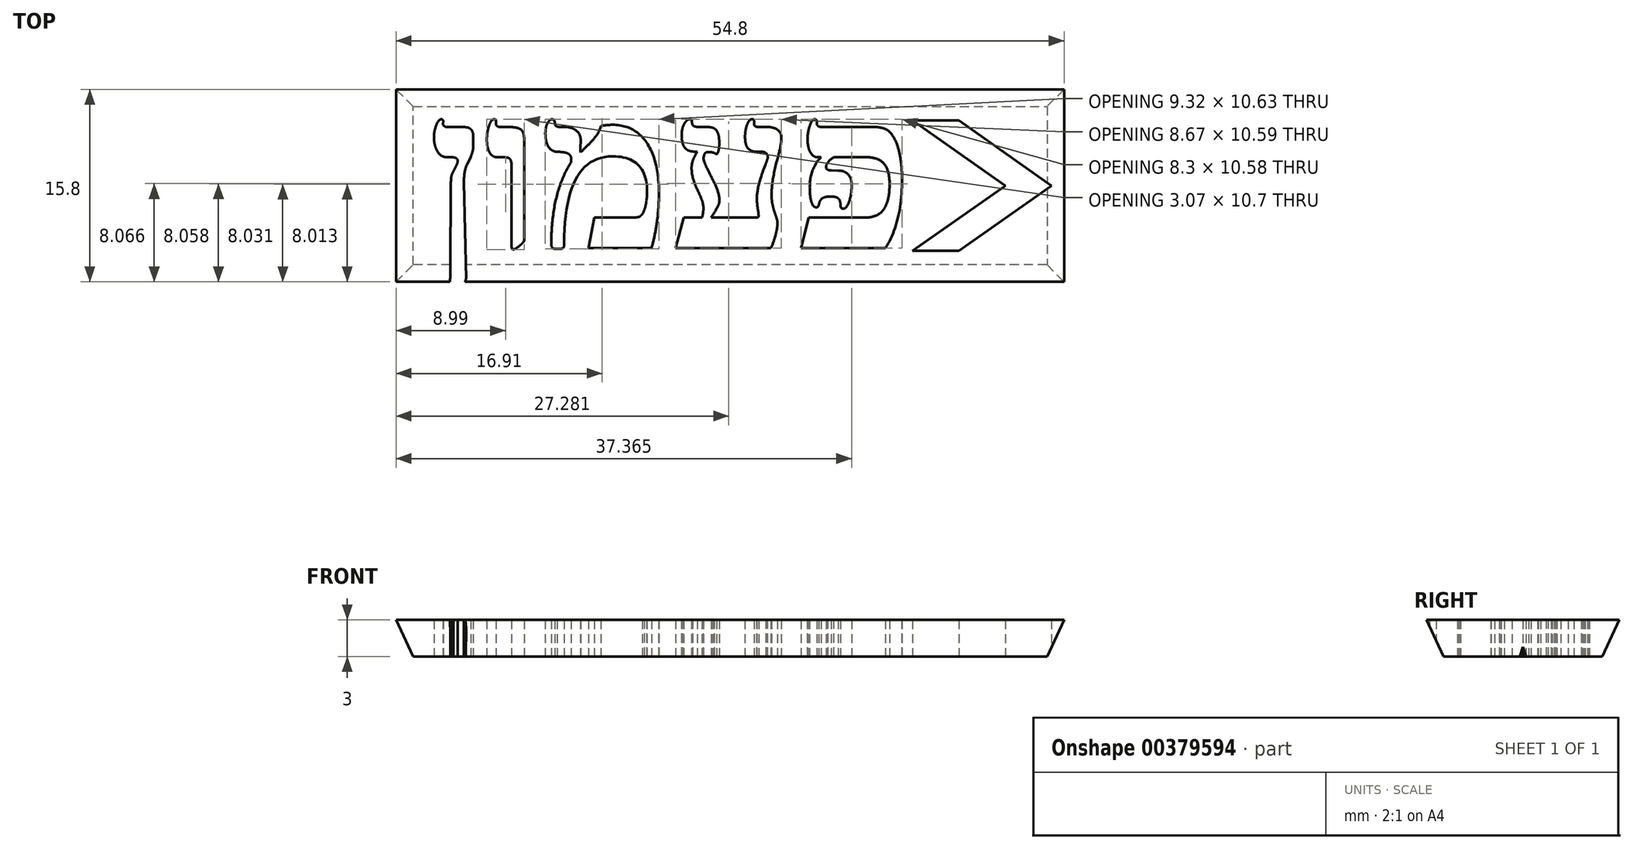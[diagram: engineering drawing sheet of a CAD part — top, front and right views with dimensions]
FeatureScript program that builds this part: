
annotation { "Feature Type Name" : "Feature", "Feature Type Description" : "" }
export const myFeature = defineFeature(function(context is Context, id is Id, definition is map)
    precondition{}
    {
        {
            var Q0;
            Q0=qCreatedBy(makeId("Top.planeOp"),FACE);
            var sketch = newSketch(context, id + "F0", { "sketchPlane" : qUnion([Q0])});
            skLineSegment(sketch, "E0.bottom", {"start": v(26, -6.5) * mm, "end": v(-26, -6.5) * mm});
            skLineSegment(sketch, "E0.top", {"start": v(26, 6.5) * mm, "end": v(-26, 6.5) * mm});
            skLineSegment(sketch, "E0.left", {"start": v(26, -6.5) * mm, "end": v(26, 6.5) * mm});
            skLineSegment(sketch, "E0.right", {"start": v(-26, -6.5) * mm, "end": v(-26, 6.5) * mm});
            skPoint(sketch, "E0.middle", {"position": v(0, 0) * mm});
            skPoint(sketch, "E1.endSnap0", {"position": v(26, 0) * mm});
            skPoint(sketch, "E2.endSnap0", {"position": v(17.9, -2.28) * mm});
            skSolve(sketch);
        }
        {
            var Q0;
            Q0=makeQuery(id+"F0.imprint","IMPRINT",FACE,{"disambiguationData":[TD([[makeQuery(id+"F0.imprint","IMPRINT",EDGE,{"derivedFrom":sQuery(id+"F0.wireOp",EDGE,"E0.bottom")}),-1.0]])]});
            var sketch = newSketch(context, id + "F1", { "sketchPlane" : qUnion([Q0])});
            skLineSegment(sketch, "E3", {"start": v(14.97, -5.36) * mm, "end": v(22.57, 0) * mm});
            skLineSegment(sketch, "E4", {"start": v(14.97, -5.36) * mm, "end": v(18.77, -5.36) * mm});
            skPoint(sketch, "E4.endSnap0", {"position": v(18.77, -2.68) * mm});
            skLineSegment(sketch, "E5", {"start": v(18.77, -5.36) * mm, "end": v(26.37, 0) * mm});
            skLineSegment(sketch, "E6.MirrorCS", {"start": v(18.77, 5.36) * mm, "end": v(26.37, 0) * mm});
            skLineSegment(sketch, "E7.MirrorCS", {"start": v(14.97, 5.36) * mm, "end": v(22.57, 0) * mm});
            skLineSegment(sketch, "E8.MirrorCS", {"start": v(14.97, 5.36) * mm, "end": v(18.77, 5.36) * mm});
            skSolve(sketch);
        }
        {
            var Q0;
            Q0=makeQuery(id+"F0.imprint","IMPRINT",FACE,{"disambiguationData":[TD([[makeQuery(id+"F0.imprint","IMPRINT",EDGE,{"derivedFrom":sQuery(id+"F0.wireOp",EDGE,"E0.bottom")}),-1.0]])]});
            var sketch = newSketch(context, id + "F2", { "sketchPlane" : qUnion([Q0])});
            skText(sketch, "E9", { "text": "ןומעפ", "fontName": "Tinos-Bold.ttf"});
            const initialGuessF2  = {"E9": [-0.02475, -0.00513, 1, 0, 0.01295]};
            skSetInitialGuess(sketch, initialGuessF2);
            skSolve(sketch);
        }
        {
            var Q0;
            Q0 = qSketchRegion(id + "F0", true);
            extrude(context, id + "F3", {"entities" : qUnion([Q0]), "depth" : 3 * mm, "hasDraft" : true, "draftAngle" : 25 * degree});
        }
        {
            var Q0;
            Q0 = qSketchRegion(id + "F2", true);
            extrude(context, id + "F4", {"entities" : qUnion([Q0]), "operationType" : NewBodyOperationType.REMOVE, "depth" : 8 * mm});
        }
        {
            var Q0;
            Q0 = qSketchRegion(id + "F1", true);
            extrude(context, id + "F5", {"entities" : qUnion([Q0]), "operationType" : NewBodyOperationType.REMOVE, "depth" : 8 * mm});
        }
    });
